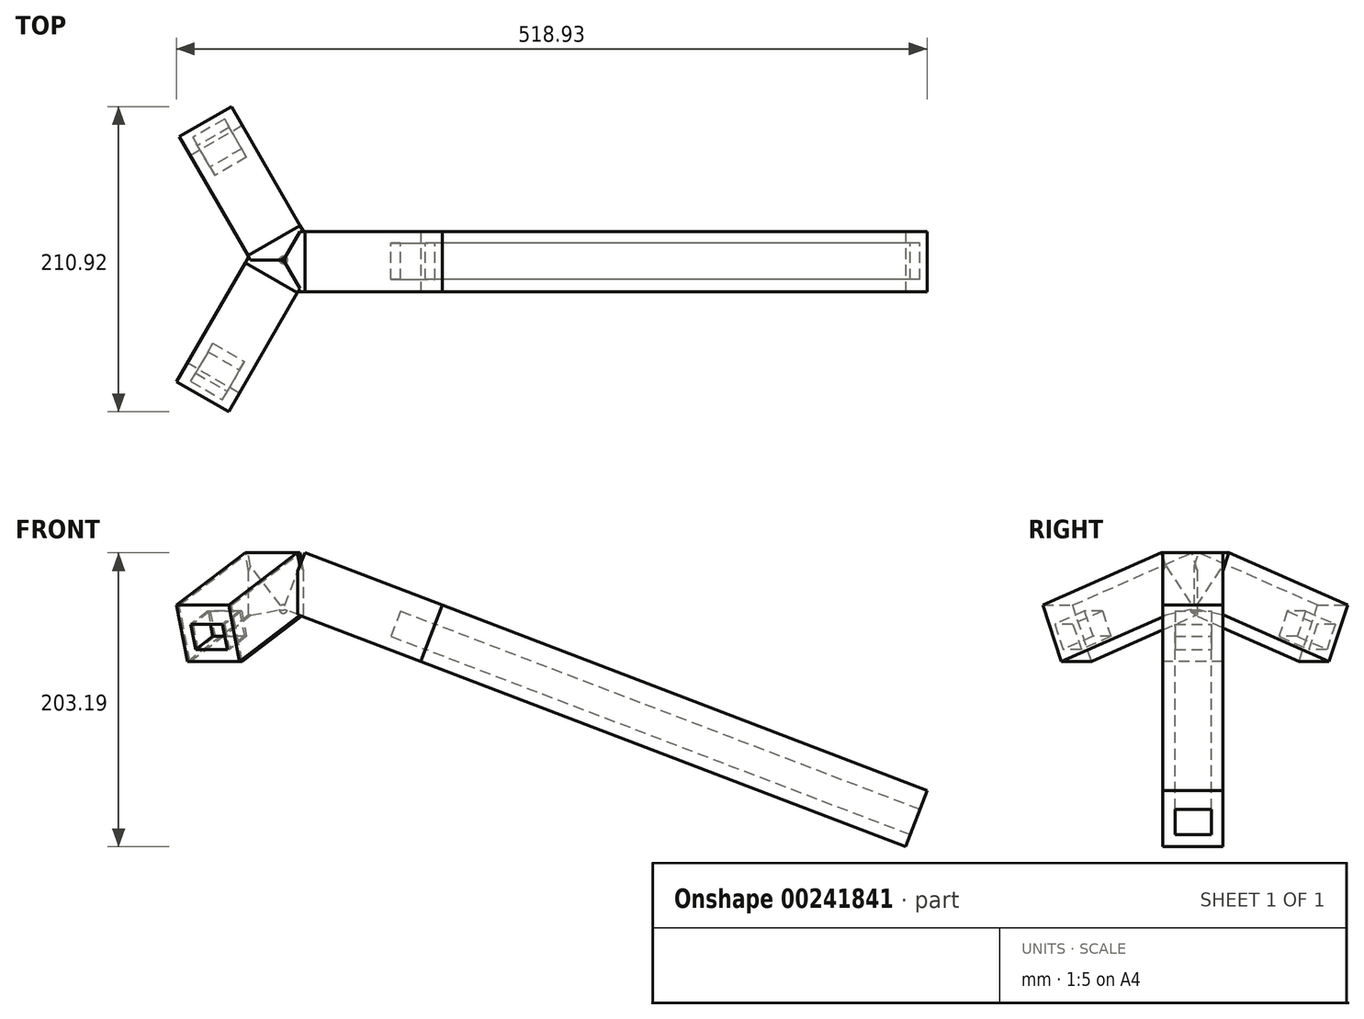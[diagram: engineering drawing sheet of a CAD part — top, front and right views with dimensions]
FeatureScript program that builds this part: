
annotation { "Feature Type Name" : "Feature", "Feature Type Description" : "" }
export const myFeature = defineFeature(function(context is Context, id is Id, definition is map)
    precondition{}
    {
        {
            var Q0;
            Q0=qCreatedBy(makeId("Right.planeOp"),FACE);
            var sketch = newSketch(context, id + "F0", { "sketchPlane" : qUnion([Q0])});
            skLineSegment(sketch, "E0.bottom", {"start": v(19.66, 0) * mm, "end": v(-21.95, 0) * mm});
            skLineSegment(sketch, "E0.top", {"start": v(19.66, 41.61) * mm, "end": v(-21.95, 41.61) * mm});
            skLineSegment(sketch, "E0.left", {"start": v(19.66, 0) * mm, "end": v(19.66, 41.61) * mm});
            skLineSegment(sketch, "E0.right", {"start": v(-21.95, 0) * mm, "end": v(-21.95, 41.61) * mm});
            skSolve(sketch);
        }
        {
            var Q0;
            Q0=makeQuery(id+"F0.imprint","IMPRINT",FACE,{"disambiguationData":[TD([[makeQuery(id+"F0.imprint","IMPRINT",EDGE,{"derivedFrom":sQuery(id+"F0.wireOp",EDGE,"E0.bottom")}),-1.0]])]});
            extrude(context, id + "F1", {"entities" : qUnion([Q0]), "depth" : 101.6 * mm});
        }
        {
            var Q0;
            Q0=makeQuery(id+"F1.opExtrude","CAP_FACE",FACE,{"disambiguationData":[OSD([sQuery(id+"F0.wireOp",EDGE,"E0.bottom"),sQuery(id+"F0.wireOp",EDGE,"E0.top"),sQuery(id+"F0.wireOp",EDGE,"E0.left"),sQuery(id+"F0.wireOp",EDGE,"E0.right")])],"isStart":false});
            var sketch = newSketch(context, id + "F2", { "sketchPlane" : qUnion([Q0])});
            skLineSegment(sketch, "E1.bottom", {"start": v(-13.45, 27.54) * mm, "end": v(11.77, 27.54) * mm});
            skLineSegment(sketch, "E1.top", {"start": v(-13.45, 8.85) * mm, "end": v(11.77, 8.85) * mm});
            skLineSegment(sketch, "E1.left", {"start": v(-13.45, 27.54) * mm, "end": v(-13.45, 8.85) * mm});
            skLineSegment(sketch, "E1.right", {"start": v(11.77, 27.54) * mm, "end": v(11.77, 8.85) * mm});
            skSolve(sketch);
        }
        {
            var Q0;
            Q0=makeQuery(id+"F2.imprint","IMPRINT",FACE,{"disambiguationData":[TD([[makeQuery(id+"F2.imprint","IMPRINT",EDGE,{"derivedFrom":sQuery(id+"F2.wireOp",EDGE,"E1.bottom")}),-1.0]])]});
            extrude(context, id + "F3", {"entities" : qUnion([Q0]), "operationType" : NewBodyOperationType.REMOVE, "oppositeDirection" : true, "depth" : 25.4 * mm});
        }
        {
            var Q0;
            Q0=makeQuery(id+"F1.opExtrude","SWEPT_BODY",BODY,{"disambiguationData":[OSD([sQuery(id+"F0.wireOp",EDGE,"E0.bottom"),sQuery(id+"F0.wireOp",EDGE,"E0.top"),sQuery(id+"F0.wireOp",EDGE,"E0.left"),sQuery(id+"F0.wireOp",EDGE,"E0.right")])]});
            var Q1;
            Q1=makeQuery(id+"F1.opExtrude","CAP_EDGE",EDGE,{"disambiguationData":[OSD([sQuery(id+"F0.wireOp",EDGE,"E0.bottom")])],"isStart":true});
            transform(context, id + "F4", {"entities" : qUnion([Q0]), "transformType" : TransformType.ROTATION, "transformAxis" : qUnion([Q1]), "angle" : 20.9 * degree, "oppositeDirection" : true, "makeCopy" : false});
        }
        {
            var Q0;
            Q0=qCreatedBy(makeId("Front.planeOp"),FACE);
            var sketch = newSketch(context, id + "F5", { "sketchPlane" : qUnion([Q0])});
            skLineSegment(sketch, "E2", {"start": v(0, 0) * mm, "end": v(0, 73.76) * mm, "construction": true});
            skSolve(sketch);
        }
        {
            var Q0;
            Q0=qCreatedBy(makeId("Top.planeOp"),FACE);
            var sketch = newSketch(context, id + "F6", { "sketchPlane" : qUnion([Q0])});
            skArc(sketch, "E3", {"start": v(0, 2.92) * mm, "mid": v(-2.92, 0) * mm, "end": v(0, -2.92) * mm});
            skLineSegment(sketch, "E4", {"start": v(0, 2.92) * mm, "end": v(0, -2.92) * mm});
            skSolve(sketch);
        }
        {
            var Q0;
            Q0=makeQuery(id+"F6.imprint","IMPRINT",FACE,{"disambiguationData":[TD([[makeQuery(id+"F6.imprint","IMPRINT",EDGE,{"derivedFrom":sQuery(id+"F6.wireOp",EDGE,"E3")}),1.0]])]});
            var Q1;
            Q1=sQuery(id+"F6.wireOp",EDGE,"E4");
            revolve(context, id + "F7", {"operationType" : NewBodyOperationType.ADD, "entities" : qUnion([Q0]), "axis" : qUnion([Q1]), "revolveType" : RevolveType.FULL});
        }
        {
            var Q0;
            Q0=makeQuery(id+"F1.opExtrude","SWEPT_BODY",BODY,{"disambiguationData":[OSD([sQuery(id+"F0.wireOp",EDGE,"E0.bottom"),sQuery(id+"F0.wireOp",EDGE,"E0.top"),sQuery(id+"F0.wireOp",EDGE,"E0.left"),sQuery(id+"F0.wireOp",EDGE,"E0.right")])]});
            var Q1;
            Q1=sQuery(id+"F5.wireOp",EDGE,"E2");
            circularPattern(context, id + "F8", {"operationType" : NewBodyOperationType.ADD, "entities" : qUnion([Q0]), "axis" : qUnion([Q1]), "angle" : 360 * degree, "instanceCount" : 3, "equalSpace" : true});
        }
        {
            var Q0;
            Q0=makeQuery(id+"F1.opExtrude","CAP_FACE",FACE,{"disambiguationData":[OSD([sQuery(id+"F0.wireOp",EDGE,"E0.bottom"),sQuery(id+"F0.wireOp",EDGE,"E0.top"),sQuery(id+"F0.wireOp",EDGE,"E0.left"),sQuery(id+"F0.wireOp",EDGE,"E0.right")])],"isStart":false});
            extrude(context, id + "F9", {"entities" : qUnion([Q0]), "depth" : 358.9 * mm});
        }
    });
